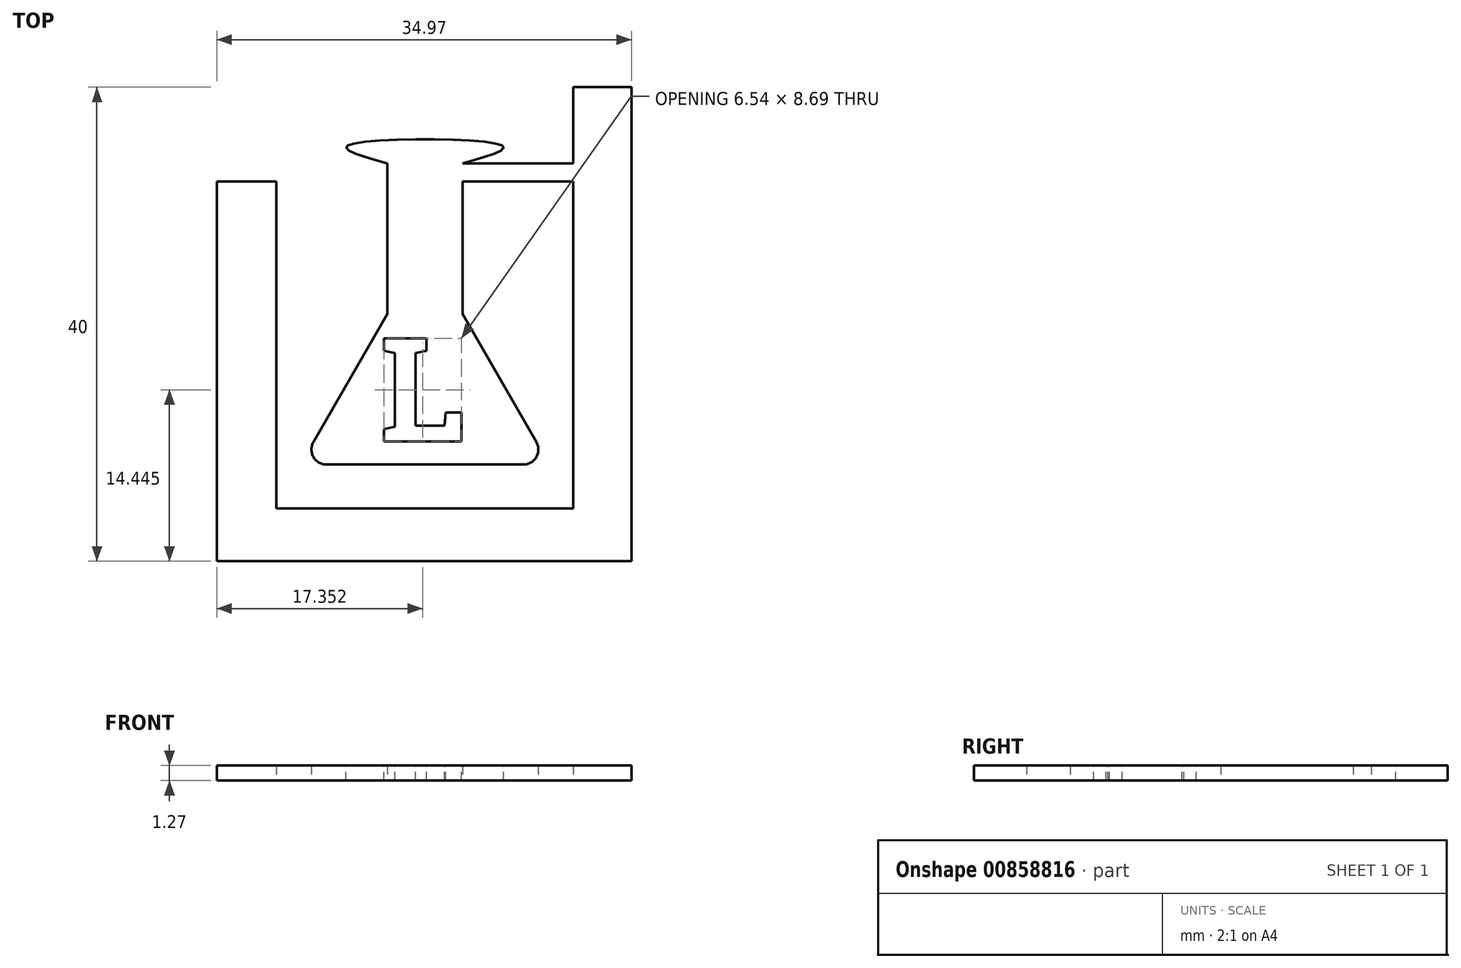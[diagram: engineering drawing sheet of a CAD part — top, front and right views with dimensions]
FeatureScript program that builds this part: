
annotation { "Feature Type Name" : "Feature", "Feature Type Description" : "" }
export const myFeature = defineFeature(function(context is Context, id is Id, definition is map)
    precondition{}
    {
        {
            var Q0;
            Q0=qCreatedBy(makeId("Top.planeOp"),FACE);
            var sketch = newSketch(context, id + "F0", { "sketchPlane" : qUnion([Q0])});
            skLineSegment(sketch, "E0.top", {"start": v(17.42, -24.66) * mm, "end": v(-17.55, -24.66) * mm});
            skLineSegment(sketch, "E0.left", {"start": v(17.42, 15.34) * mm, "end": v(17.42, -24.66) * mm});
            skLineSegment(sketch, "E0.right", {"start": v(-17.55, -0.21) * mm, "end": v(-17.55, -24.66) * mm});
            skLineSegment(sketch, "E1.top", {"start": v(12.52, -20.21) * mm, "end": v(-12.55, -20.21) * mm});
            skLineSegment(sketch, "E1.right", {"start": v(-12.55, -0.21) * mm, "end": v(-12.55, -20.21) * mm});
            skLineSegment(sketch, "E2.trimOffspring", {"start": v(12.52, 3.19) * mm, "end": v(12.52, -20.21) * mm});
            skPoint(sketch, "E3.MirrorCS.end.orphan", {"position": v(17.5, 16.1) * mm});
            skPoint(sketch, "E3.MirrorCS.start.orphan", {"position": v(12.5, 15.55) * mm});
            skLineSegment(sketch, "E4", {"start": v(12.52, 15.34) * mm, "end": v(17.42, 15.34) * mm});
            skPoint(sketch, "E5.MirrorCS.start.orphan", {"position": v(17.5, 15.55) * mm});
            skLineSegment(sketch, "E6", {"start": v(12.52, 15.34) * mm, "end": v(12.52, 10.97) * mm});
            skLineSegment(sketch, "E7.trimOffspring", {"start": v(12.52, 7.37) * mm, "end": v(12.52, 3.19) * mm});
            skLineSegment(sketch, "E8", {"start": v(12.52, 10.97) * mm, "end": v(12.52, 8.9) * mm});
            skLineSegment(sketch, "E9.left", {"start": v(3.18, 7.37) * mm, "end": v(3.18, -3.8) * mm});
            skLineSegment(sketch, "E9.right", {"start": v(-3.18, 8.89) * mm, "end": v(-3.18, -3.8) * mm});
            skPoint(sketch, "E9.middle", {"position": v(0, 2.54) * mm});
            skLineSegment(sketch, "E10", {"start": v(-3.18, -3.8) * mm, "end": v(-9.4, -14.6) * mm});
            skLineSegment(sketch, "E11.MirrorCS", {"start": v(3.17, -3.8) * mm, "end": v(9.4, -14.6) * mm});
            skLineSegment(sketch, "E12", {"start": v(-8.3, -16.51) * mm, "end": v(8.3, -16.5) * mm});
            skPoint(sketch, "E13.visualSharp", {"position": v(10.5, -16.51) * mm});
            skArc(sketch, "E13.filletArc", {"start": v(8.3, -16.5) * mm, "mid": v(9.4, -15.88) * mm, "end": v(9.4, -14.6) * mm});
            skPoint(sketch, "E14.visualSharp", {"position": v(-10.5, -16.51) * mm});
            skArc(sketch, "E14.filletArc", {"start": v(-9.4, -14.6) * mm, "mid": v(-9.4, -15.88) * mm, "end": v(-8.3, -16.5) * mm});
            skPoint(sketch, "E15.start.orphan", {"position": v(-2.32, 0) * mm});
            skFitSpline(sketch, "E16", {"points": [v(-3.18, 8.9) * mm, v(-6.53, 10.41) * mm, v(6.53, 10.41) * mm, v(3.18, 8.9) * mm], "startDerivative": vector(-23.3, 6.7) * mm, "endDerivative": vector(-23.3, -6.7) * mm});
            skLineSegment(sketch, "E17", {"start": v(3.17, 7.37) * mm, "end": v(12.52, 7.37) * mm});
            skLineSegment(sketch, "E18", {"start": v(3.18, 8.9) * mm, "end": v(12.52, 8.9) * mm});
            skLineSegment(sketch, "E19.left", {"start": v(-17.55, -0.21) * mm, "end": v(-17.55, 7.37) * mm});
            skLineSegment(sketch, "E20.trimOffspring", {"start": v(-13.65, 7.37) * mm, "end": v(-17.64, 7.37) * mm});
            skLineSegment(sketch, "E21.top", {"start": v(-12.55, 7.37) * mm, "end": v(-13.65, 7.37) * mm});
            skLineSegment(sketch, "E21.left", {"start": v(-12.55, -0.21) * mm, "end": v(-12.55, 7.37) * mm});
            skLineSegment(sketch, "E22", {"start": v(0, -16.51) * mm, "end": v(0, -3.8) * mm, "construction": true});
            skPoint(sketch, "E23", {"position": v(0, -10.16) * mm});
            skSolve(sketch);
        }
        {
            var Q0;
            Q0=makeQuery(id+"F0.imprint","IMPRINT",FACE,{"disambiguationData":[TD([[makeQuery(id+"F0.imprint","IMPRINT",EDGE,{"derivedFrom":sQuery(id+"F0.wireOp",EDGE,"E0.top")}),-1.0]])]});
            var Q1;
            {var subQ0=sQuery(id+"F0.wireOp",EDGE,"FKejiANf-u82S-7BPr-4an4-q4Ka4m4IZFMA");var subQ1=makeQuery(id+"F0.imprint","INTERSECT",VERTEX,{"derivedFrom":[sQuery(id+"F0.wireOp",EDGE,"1SfU6YIB-wvzm-6zBe-5eDS-HKFIA9QaUayn"),subQ0]});Q1=makeQuery(id+"F0.imprint","IMPRINT",FACE,{"disambiguationData":[TD([[makeQuery(id+"F0.imprint","IMPRINT",EDGE,{"disambiguationData":[TD([[subQ1,1.0]])],"derivedFrom":subQ0}),1.0]])]});}
            extrude(context, id + "F1", {"entities" : qUnion([Q0, Q1]), "depth" : 1.27 * mm, "offsetDistance" : 25.4 * mm});
        }
        {
            var Q0;
            Q0=makeQuery(id+"F1.opExtrude","CAP_FACE",FACE,{"disambiguationData":[OSD([sQuery(id+"F0.wireOp",EDGE,"E0.top"),sQuery(id+"F0.wireOp",EDGE,"E0.left"),sQuery(id+"F0.wireOp",EDGE,"E0.right"),sQuery(id+"F0.wireOp",EDGE,"E1.top"),sQuery(id+"F0.wireOp",EDGE,"E1.right"),sQuery(id+"F0.wireOp",EDGE,"1SfU6YIB-wvzm-6zBe-5eDS-HKFIA9QaUayn"),sQuery(id+"F0.wireOp",EDGE,"sM1Sgktc-x2VY-oS3Z-5OfG-QNgHwikTJDgL"),sQuery(id+"F0.wireOp",EDGE,"7EqO3XEm-McEN-PWzp-HPdO-5mDO97qVc4eW"),sQuery(id+"F0.wireOp",EDGE,"BdKeHqo0-FdcT-Rb85-6iZA-lVtgPkFKthWV"),sQuery(id+"F0.wireOp",EDGE,"FKejiANf-u82S-7BPr-4an4-q4Ka4m4IZFMA"),sQuery(id+"F0.wireOp",EDGE,"eK1Uujpq-Df3w-NQqX-Gc2k-lf4LO3mh3muX"),sQuery(id+"F0.wireOp",EDGE,"9dokPukG-NNzw-ETl1-5EZM-OfzmBowc8QZ2"),sQuery(id+"F0.wireOp",EDGE,"89ef536c-63d7-428c-8d95-022694007808.trimOffspring"),sQuery(id+"F0.wireOp",EDGE,"e37d3fe4-c149-4dc4-956f-d1983d31f44f.trimOffspring"),sQuery(id+"F0.wireOp",EDGE,"E2.trimOffspring"),sQuery(id+"F0.wireOp",EDGE,"eCGh251j-4Mt1-Y2Ib-rAlh-B7rz0UIJvHUj"),sQuery(id+"F0.wireOp",EDGE,"E4")])],"isStart":false});
            var sketch = newSketch(context, id + "F2", { "sketchPlane" : qUnion([Q0])});
            skText(sketch, "E24", { "text": "L\n", "fontName": "RobotoSlab-Bold.ttf"});
            skPoint(sketch, "E25", {"position": v(0, -10.16) * mm});
            const initialGuessF2  = {"E24": [-0.0038, -0.01456, 1, 0, 0.0088]};
            skSetInitialGuess(sketch, initialGuessF2);
            skSolve(sketch);
        }
        {
            var Q0;
            Q0=makeQuery(id+"F2.imprint","IMPRINT",FACE,{"disambiguationData":[TD([[makeQuery(id+"F2.imprint","IMPRINT",EDGE,{"derivedFrom":sQuery(id+"F2.wireOp",EDGE,"E24.sketch_text.stroke-16")}),-1.0]])]});
            var Q1;
            Q1=makeQuery(id+"F2.imprint","IMPRINT",FACE,{"disambiguationData":[TD([[makeQuery(id+"F2.imprint","IMPRINT",EDGE,{"derivedFrom":sQuery(id+"F2.wireOp",EDGE,"E24.sketch_text.stroke-0")}),-1.0]])]});
            extrude(context, id + "F3", {"entities" : qUnion([Q0, Q1]), "operationType" : NewBodyOperationType.REMOVE, "oppositeDirection" : true, "depth" : 25.4 * mm, "offsetDistance" : 25.4 * mm});
        }
    });
